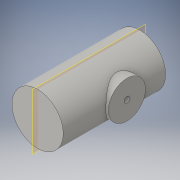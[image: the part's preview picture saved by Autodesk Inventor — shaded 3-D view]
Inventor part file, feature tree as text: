
AUTODESK INVENTOR PART (.ipt)
format: ipt  version: 2016 (Build 200138000, 138)  size: 108,032 bytes
history: native  units: in
note: dims shown in document units (in); Inventor stores cm internally (conversion verified against a paired STEP export)
features: extrude x3, sketch x3
ambient origin geometry x8: Origin, YZ Plane, XZ Plane, XY Plane, X Axis, Y Axis, Z Axis, Center Point
bodies: Solid1 (feature_tree)
feature tree (6):
  extrude  "Extrusion1"  Depth=2.129in TaperAngle=0.0deg
  extrude  "Extrusion2"  Depth=0.583in TaperAngle=0.0deg
  extrude  "Extrusion3"  Depth=0.583in TaperAngle=0.0deg
  sketch  "Sketch1"  dims[d0=1.065in d1=2.129in d2=0.0in]
  sketch  "Sketch2"  dims[d3=0.772in d4=0.583in d5=0.0in]
  sketch  "Sketch3"  dims[d6=0.1181in d7=0.583in d8=0.0in]
